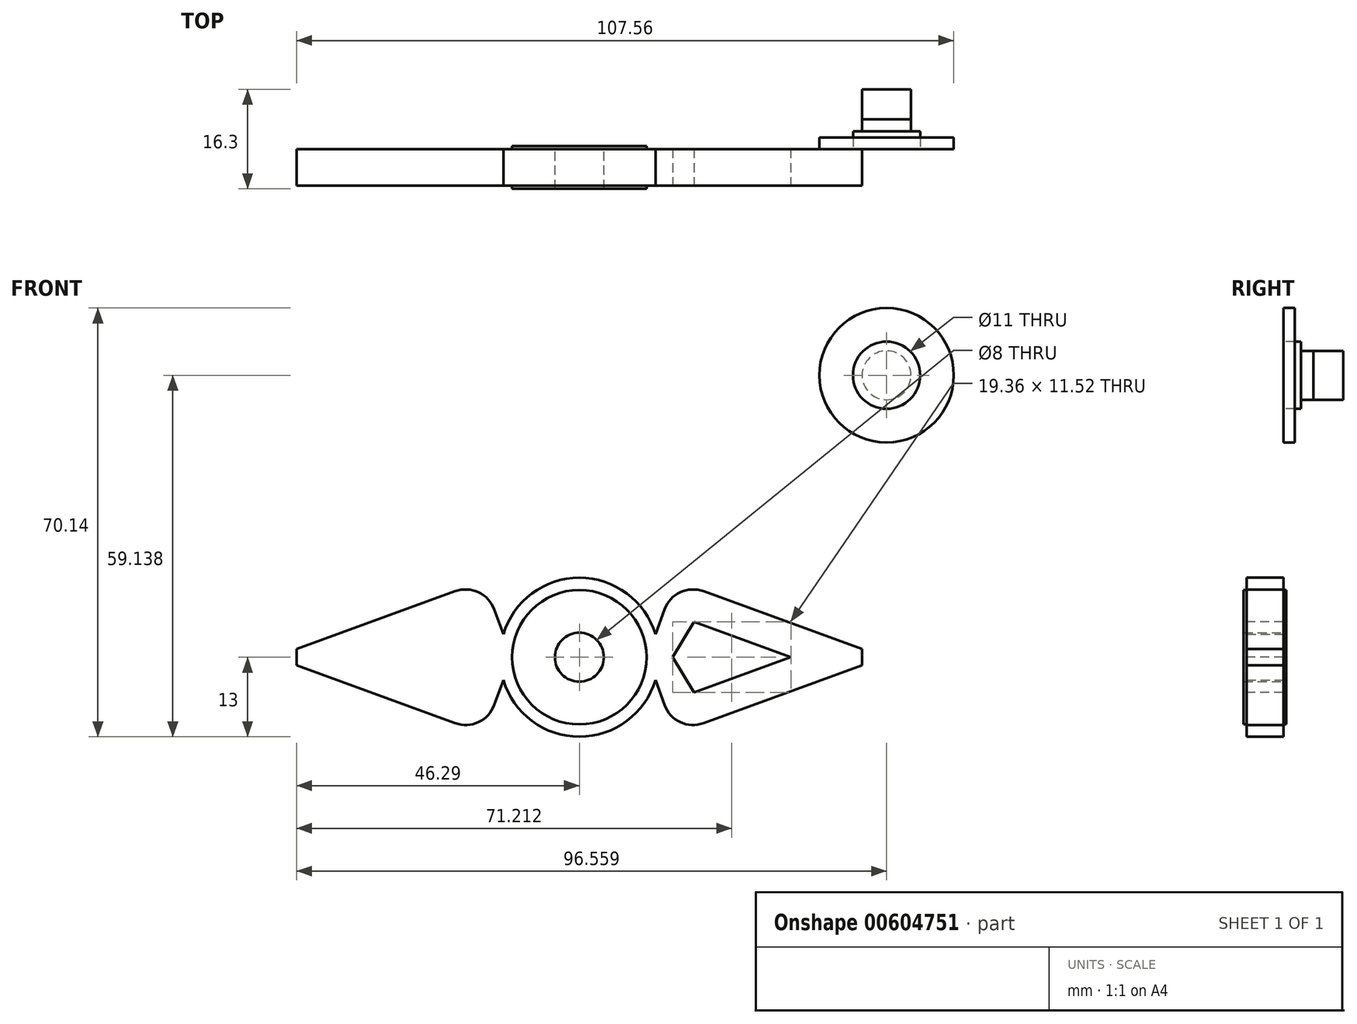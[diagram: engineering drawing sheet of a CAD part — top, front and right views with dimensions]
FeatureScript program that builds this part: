
annotation { "Feature Type Name" : "Feature", "Feature Type Description" : "" }
export const myFeature = defineFeature(function(context is Context, id is Id, definition is map)
    precondition{}
    {
        {
            var Q0;
            Q0=qCreatedBy(makeId("Front.planeOp"),FACE);
            var sketch = newSketch(context, id + "F0", { "sketchPlane" : qUnion([Q0])});
            skCircle(sketch, "E0", {"center": v(0, 0) * mm, "radius": 11 * mm});
            skCircle(sketch, "E1", {"center": v(0, 0) * mm, "radius": 13 * mm});
            skLineSegment(sketch, "E2", {"start": v(-12.45, 3.75) * mm, "end": v(-15.63, 12.5) * mm});
            skLineSegment(sketch, "E3", {"start": v(-15.63, 12.5) * mm, "end": v(-50, 0) * mm});
            skLineSegment(sketch, "E4.MirrorCS", {"start": v(-15.63, -12.5) * mm, "end": v(-50, 0) * mm});
            skLineSegment(sketch, "E5.MirrorCS", {"start": v(-12.45, -3.75) * mm, "end": v(-15.63, -12.5) * mm});
            skLineSegment(sketch, "E6.MirrorCS", {"start": v(12.45, 3.75) * mm, "end": v(15.63, 12.5) * mm});
            skLineSegment(sketch, "E7.MirrorCS", {"start": v(15.63, 12.5) * mm, "end": v(50, 0) * mm});
            skLineSegment(sketch, "E8.MirrorCS", {"start": v(15.63, -12.5) * mm, "end": v(50, 0) * mm});
            skLineSegment(sketch, "E9.MirrorCS", {"start": v(12.45, -3.75) * mm, "end": v(15.63, -12.5) * mm});
            skCircle(sketch, "E10", {"center": v(0, 0) * mm, "radius": 9.5 * mm});
            skCircle(sketch, "E11", {"center": v(0, 0) * mm, "radius": 5.1 * mm});
            skCircle(sketch, "E12", {"center": v(0, 0) * mm, "radius": 4 * mm});
            skLineSegment(sketch, "E13", {"start": v(46.29, 1.35) * mm, "end": v(46.29, -1.35) * mm});
            skLineSegment(sketch, "E14.MirrorCS", {"start": v(-46.29, 1.35) * mm, "end": v(-46.29, -1.35) * mm});
            skSolve(sketch);
        }
        {
            var Q0;
            {var subQ1=sQuery(id+"F0.wireOp",EDGE,"E6.MirrorCS");Q0=makeQuery(id+"F0.imprint","IMPRINT",FACE,{"disambiguationData":[TD([[makeQuery(id+"F0.imprint","IMPRINT",EDGE,{"derivedFrom":subQ1}),-1.0]])]});}
            var Q1;
            Q1=makeQuery(id+"F0.imprint","IMPRINT",FACE,{"disambiguationData":[TD([[makeQuery(id+"F0.imprint","IMPRINT",EDGE,{"derivedFrom":sQuery(id+"F0.wireOp",EDGE,"E0")}),-1.0]])]});
            var Q2;
            {var subQ4=sQuery(id+"F0.wireOp",EDGE,"E2");Q2=makeQuery(id+"F0.imprint","IMPRINT",FACE,{"disambiguationData":[TD([[makeQuery(id+"F0.imprint","IMPRINT",EDGE,{"derivedFrom":subQ4}),1.0]])]});}
            extrude(context, id + "F1", {"entities" : qUnion([Q0, Q1, Q2]), "depth" : 6 * mm, "offsetDistance" : 25 * mm});
        }
        {
            var Q0;
            Q0=makeQuery(id+"F1.opExtrude","SWEPT_EDGE",EDGE,{"disambiguationData":[OSD([sQuery(id+"F0.wireOp",EDGE,"E6.MirrorCS"),sQuery(id+"F0.wireOp",EDGE,"E7.MirrorCS")])]});
            var Q1;
            Q1=makeQuery(id+"F1.opExtrude","SWEPT_EDGE",EDGE,{"disambiguationData":[OSD([sQuery(id+"F0.wireOp",EDGE,"E8.MirrorCS"),sQuery(id+"F0.wireOp",EDGE,"E9.MirrorCS")])]});
            var Q2;
            Q2=makeQuery(id+"F1.opExtrude","SWEPT_EDGE",EDGE,{"disambiguationData":[OSD([sQuery(id+"F0.wireOp",EDGE,"E4.MirrorCS"),sQuery(id+"F0.wireOp",EDGE,"E5.MirrorCS")])]});
            var Q3;
            Q3=makeQuery(id+"F1.opExtrude","SWEPT_EDGE",EDGE,{"disambiguationData":[OSD([sQuery(id+"F0.wireOp",EDGE,"E2"),sQuery(id+"F0.wireOp",EDGE,"E3")])]});
            fillet(context, id + "F2", {"entities" : qUnion([Q0, Q1, Q2, Q3]), "radius" : 5 * mm, "tangentPropagation" : true, "allowEdgeOverflow" : false});
        }
        {
            var Q0;
            Q0=makeQuery(id+"F1.opExtrude","CAP_FACE",FACE,{"disambiguationData":[OSD([sQuery(id+"F0.wireOp",EDGE,"E0"),sQuery(id+"F0.wireOp",EDGE,"E1"),sQuery(id+"F0.wireOp",EDGE,"E2"),sQuery(id+"F0.wireOp",EDGE,"E3"),sQuery(id+"F0.wireOp",EDGE,"E4.MirrorCS"),sQuery(id+"F0.wireOp",EDGE,"E5.MirrorCS"),sQuery(id+"F0.wireOp",EDGE,"E6.MirrorCS"),sQuery(id+"F0.wireOp",EDGE,"E7.MirrorCS"),sQuery(id+"F0.wireOp",EDGE,"E8.MirrorCS"),sQuery(id+"F0.wireOp",EDGE,"E9.MirrorCS"),sQuery(id+"F0.wireOp",EDGE,"E13"),sQuery(id+"F0.wireOp",EDGE,"E14.MirrorCS")])],"isStart":false});
            var sketch = newSketch(context, id + "F3", { "sketchPlane" : qUnion([Q0])});
            skLineSegment(sketch, "E15", {"start": v(-18.77, 5.76) * mm, "end": v(-34.6, 0) * mm});
            skLineSegment(sketch, "E16", {"start": v(-18.77, 5.76) * mm, "end": v(-15.24, 0) * mm});
            skLineSegment(sketch, "E17.MirrorCS", {"start": v(-18.77, -5.76) * mm, "end": v(-34.6, 0) * mm});
            skLineSegment(sketch, "E18.MirrorCS", {"start": v(-18.77, -5.76) * mm, "end": v(-15.24, 0) * mm});
            skLineSegment(sketch, "E19.MirrorCS", {"start": v(18.77, 5.76) * mm, "end": v(34.6, 0) * mm});
            skLineSegment(sketch, "E20.MirrorCS", {"start": v(18.77, -5.76) * mm, "end": v(34.6, 0) * mm});
            skLineSegment(sketch, "E21.MirrorCS", {"start": v(18.77, -5.76) * mm, "end": v(15.24, 0) * mm});
            skLineSegment(sketch, "E22.MirrorCS", {"start": v(18.77, 5.76) * mm, "end": v(15.24, 0) * mm});
            skSolve(sketch);
        }
        {
            var Q0;
            Q0=makeQuery(id+"F3.imprint","IMPRINT",FACE,{"disambiguationData":[TD([[makeQuery(id+"F3.imprint","IMPRINT",EDGE,{"derivedFrom":sQuery(id+"F3.wireOp",EDGE,"E15")}),1.0]])]});
            var sketch = newSketch(context, id + "F4", { "sketchPlane" : qUnion([Q0])});
            skSolve(sketch);
        }
        {
            var Q0;
            Q0 = qSketchRegion(id + "F4", true);
            var Q1;
            Q1=makeQuery(id+"F3.imprint","IMPRINT",FACE,{"disambiguationData":[TD([[makeQuery(id+"F3.imprint","IMPRINT",EDGE,{"derivedFrom":sQuery(id+"F3.wireOp",EDGE,"E19.MirrorCS")}),-1.0]])]});
            var Q2;
            Q2=makeQuery(id+"F4.imprint","IMPRINT",FACE,{"disambiguationData":[TD([[makeQuery(id+"F4.imprint","IMPRINT",EDGE,{"derivedFrom":makeQuery(id+"F3.imprint","IMPRINT",EDGE,{"derivedFrom":sQuery(id+"F3.wireOp",EDGE,"E15")})}),1.0]])]});
            extrude(context, id + "F5", {"entities" : qUnion([Q0, Q1, Q2]), "operationType" : NewBodyOperationType.REMOVE, "oppositeDirection" : true, "depth" : 25 * mm, "offsetDistance" : 25 * mm});
        }
        {
            var Q0;
            Q0=qCreatedBy(makeId("Front.planeOp"),FACE);
            var sketch = newSketch(context, id + "F6", { "sketchPlane" : qUnion([Q0])});
            skCircle(sketch, "E23", {"center": v(50.27, 46.14) * mm, "radius": 4 * mm});
            skSolve(sketch);
        }
        {
            var Q0;
            Q0=qCreatedBy(makeId("Front.planeOp"),FACE);
            var sketch = newSketch(context, id + "F7", { "sketchPlane" : qUnion([Q0])});
            skCircle(sketch, "E24", {"center": v(0, 0) * mm, "radius": 4 * mm});
            skCircle(sketch, "E25", {"center": v(0, 0) * mm, "radius": 5.1 * mm});
            skSolve(sketch);
        }
        {
            var Q0;
            Q0=makeQuery(id+"F0.imprint","IMPRINT",FACE,{"disambiguationData":[TD([[makeQuery(id+"F0.imprint","IMPRINT",EDGE,{"derivedFrom":sQuery(id+"F0.wireOp",EDGE,"E0")}),1.0]])]});
            var Q1;
            Q1=makeQuery(id+"F0.imprint","IMPRINT",FACE,{"disambiguationData":[TD([[makeQuery(id+"F0.imprint","IMPRINT",EDGE,{"derivedFrom":sQuery(id+"F0.wireOp",EDGE,"E10")}),1.0]])]});
            var Q2;
            Q2=makeQuery(id+"F0.imprint","IMPRINT",FACE,{"disambiguationData":[TD([[makeQuery(id+"F0.imprint","IMPRINT",EDGE,{"derivedFrom":sQuery(id+"F0.wireOp",EDGE,"E11")}),1.0]])]});
            var Q3;
            Q3 = qSketchRegion(id + "F7", true);
            extrude(context, id + "F8", {"entities" : qUnion([Q0, Q1, Q2, Q3]), "operationType" : NewBodyOperationType.ADD, "depth" : 6.5 * mm, "offsetDistance" : 25 * mm});
        }
        {
            var Q0;
            Q0=makeQuery(id+"F0.imprint","IMPRINT",FACE,{"disambiguationData":[TD([[makeQuery(id+"F0.imprint","IMPRINT",EDGE,{"derivedFrom":sQuery(id+"F0.wireOp",EDGE,"E0")}),1.0]])]});
            var Q1;
            Q1=makeQuery(id+"F0.imprint","IMPRINT",FACE,{"disambiguationData":[TD([[makeQuery(id+"F0.imprint","IMPRINT",EDGE,{"derivedFrom":sQuery(id+"F0.wireOp",EDGE,"E10")}),1.0]])]});
            var Q2;
            Q2=makeQuery(id+"F0.imprint","IMPRINT",FACE,{"disambiguationData":[TD([[makeQuery(id+"F0.imprint","IMPRINT",EDGE,{"derivedFrom":sQuery(id+"F0.wireOp",EDGE,"E11")}),1.0]])]});
            extrude(context, id + "F9", {"entities" : qUnion([Q0, Q1, Q2]), "operationType" : NewBodyOperationType.ADD, "oppositeDirection" : true, "depth" : 0.5 * mm, "offsetDistance" : 25 * mm});
        }
        {
            var Q0;
            Q0=qCreatedBy(makeId("Front.planeOp"),FACE);
            var sketch = newSketch(context, id + "F10", { "sketchPlane" : qUnion([Q0])});
            skCircle(sketch, "E26", {"center": v(50.27, 46.14) * mm, "radius": 11 * mm});
            skCircle(sketch, "E27", {"center": v(50.27, 46.14) * mm, "radius": 5.5 * mm});
            skSolve(sketch);
        }
        {
            var Q0;
            Q0=makeQuery(id+"F6.imprint","IMPRINT",FACE,{"disambiguationData":[TD([[makeQuery(id+"F6.imprint","IMPRINT",EDGE,{"derivedFrom":sQuery(id+"F6.wireOp",EDGE,"E23")}),1.0]])]});
            extrude(context, id + "F11", {"entities" : qUnion([Q0]), "oppositeDirection" : true, "depth" : 4.9 * mm, "offsetDistance" : 25 * mm});
        }
        {
            var Q0;
            Q0=makeQuery(id+"F11.opExtrude","CAP_FACE",FACE,{"disambiguationData":[OSD([sQuery(id+"F6.wireOp",EDGE,"E23")])],"isStart":false});
            extrude(context, id + "F12", {"entities" : qUnion([Q0]), "depth" : 4.9 * mm, "offsetDistance" : 25 * mm});
        }
        {
            var Q0;
            Q0=makeQuery(id+"F10.imprint","IMPRINT",FACE,{"disambiguationData":[TD([[makeQuery(id+"F10.imprint","IMPRINT",EDGE,{"derivedFrom":sQuery(id+"F10.wireOp",EDGE,"E27")}),1.0]])]});
            extrude(context, id + "F13", {"entities" : qUnion([Q0]), "operationType" : NewBodyOperationType.ADD, "oppositeDirection" : true, "depth" : 2.9 * mm, "offsetDistance" : 25 * mm});
        }
        {
            var Q0;
            Q0=makeQuery(id+"F10.imprint","IMPRINT",FACE,{"disambiguationData":[TD([[makeQuery(id+"F10.imprint","IMPRINT",EDGE,{"derivedFrom":sQuery(id+"F10.wireOp",EDGE,"E26")}),1.0]])]});
            extrude(context, id + "F14", {"entities" : qUnion([Q0]), "oppositeDirection" : true, "depth" : 1.9 * mm, "offsetDistance" : 25 * mm});
        }
    });
